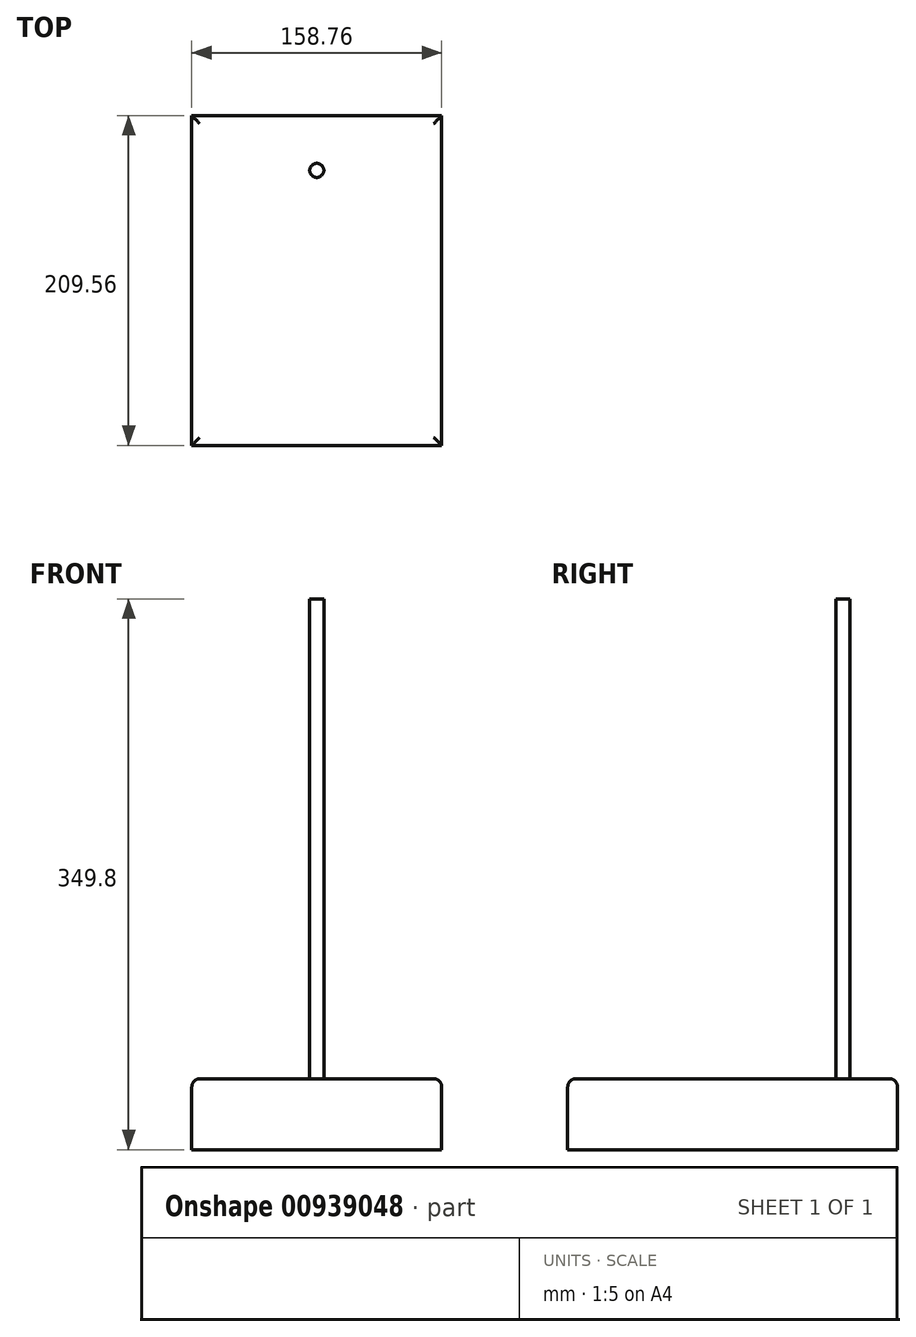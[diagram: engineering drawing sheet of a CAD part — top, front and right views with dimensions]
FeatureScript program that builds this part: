
annotation { "Feature Type Name" : "Feature", "Feature Type Description" : "" }
export const myFeature = defineFeature(function(context is Context, id is Id, definition is map)
    precondition{}
    {
        {
            var Q0;
            Q0=qCreatedBy(makeId("Top.planeOp"),FACE);
            var sketch = newSketch(context, id + "F0", { "sketchPlane" : qUnion([Q0])});
            skLineSegment(sketch, "E0.bottom", {"start": v(79.38, 104.77) * mm, "end": v(-79.38, 104.77) * mm});
            skLineSegment(sketch, "E0.top", {"start": v(79.38, -104.78) * mm, "end": v(-79.38, -104.78) * mm});
            skLineSegment(sketch, "E0.left", {"start": v(79.38, 104.78) * mm, "end": v(79.38, -104.78) * mm});
            skLineSegment(sketch, "E0.right", {"start": v(-79.38, 104.78) * mm, "end": v(-79.38, -104.78) * mm});
            skPoint(sketch, "E0.middle", {"position": v(0, 0) * mm});
            skSolve(sketch);
        }
        {
            var Q0;
            Q0 = qSketchRegion(id + "F0", true);
            extrude(context, id + "F1", {"entities" : qUnion([Q0]), "depth" : 45 * mm, "offsetDistance" : 25.4 * mm});
        }
        {
            var Q0;
            Q0=makeQuery(id+"F1.opExtrude","CAP_FACE",FACE,{"disambiguationData":[OSD([sQuery(id+"F0.wireOp",EDGE,"E0.bottom"),sQuery(id+"F0.wireOp",EDGE,"E0.top"),sQuery(id+"F0.wireOp",EDGE,"E0.left"),sQuery(id+"F0.wireOp",EDGE,"E0.right")])],"isStart":false});
            var sketch = newSketch(context, id + "F2", { "sketchPlane" : qUnion([Q0])});
            skLineSegment(sketch, "E1", {"start": v(0, 104.77) * mm, "end": v(0, 0) * mm});
            skCircle(sketch, "E2", {"center": v(0, 0) * mm, "radius": 4.5 * mm});
            skLineSegment(sketch, "E3", {"start": v(0, 104.77) * mm, "end": v(0, 69.94) * mm});
            skCircle(sketch, "E4", {"center": v(0, 69.94) * mm, "radius": 4.5 * mm});
            skSolve(sketch);
        }
        {
            var Q0;
            {var subQ0=sQuery(id+"F2.wireOp",EDGE,"E3");var subQ1=sQuery(id+"F2.wireOp",EDGE,"E1");var subQ2=makeQuery(id+"F2.imprint","INTERSECT",VERTEX,{"derivedFrom":[subQ1,subQ0]});Q0=makeQuery(id+"F2.imprint","IMPRINT",FACE,{"disambiguationData":[TD([[makeQuery(id+"F2.imprint","IMPRINT",EDGE,{"disambiguationData":[TD([[subQ2,-1.0]])],"derivedFrom":subQ1}),-1.0]])]});}
            var Q1;
            {var subQ0=sQuery(id+"F2.wireOp",EDGE,"E3");var subQ1=sQuery(id+"F2.wireOp",EDGE,"E1");var subQ2=makeQuery(id+"F2.imprint","INTERSECT",VERTEX,{"derivedFrom":[subQ1,subQ0]});Q1=makeQuery(id+"F2.imprint","IMPRINT",FACE,{"disambiguationData":[TD([[makeQuery(id+"F2.imprint","IMPRINT",EDGE,{"disambiguationData":[TD([[subQ2,-1.0]])],"derivedFrom":subQ1}),1.0]])]});}
            extrude(context, id + "F3", {"entities" : qUnion([Q0, Q1]), "operationType" : NewBodyOperationType.ADD, "depth" : 304.8 * mm, "offsetDistance" : 25.4 * mm});
        }
        {
            var Q0;
            Q0=makeQuery(id+"F1.opExtrude","CAP_EDGE",EDGE,{"disambiguationData":[OSD([sQuery(id+"F0.wireOp",EDGE,"E0.left")])],"isStart":false});
            var Q1;
            Q1=makeQuery(id+"F1.opExtrude","CAP_EDGE",EDGE,{"disambiguationData":[OSD([sQuery(id+"F0.wireOp",EDGE,"E0.top")])],"isStart":false});
            var Q2;
            Q2=makeQuery(id+"F1.opExtrude","CAP_EDGE",EDGE,{"disambiguationData":[OSD([sQuery(id+"F0.wireOp",EDGE,"E0.right")])],"isStart":false});
            var Q3;
            Q3=makeQuery(id+"F1.opExtrude","CAP_EDGE",EDGE,{"disambiguationData":[OSD([sQuery(id+"F0.wireOp",EDGE,"E0.bottom")])],"isStart":false});
            fillet(context, id + "F4", {"entities" : qUnion([Q0, Q1, Q2, Q3]), "radius" : 5.08 * mm, "tangentPropagation" : true, "allowEdgeOverflow" : false});
        }
    });
